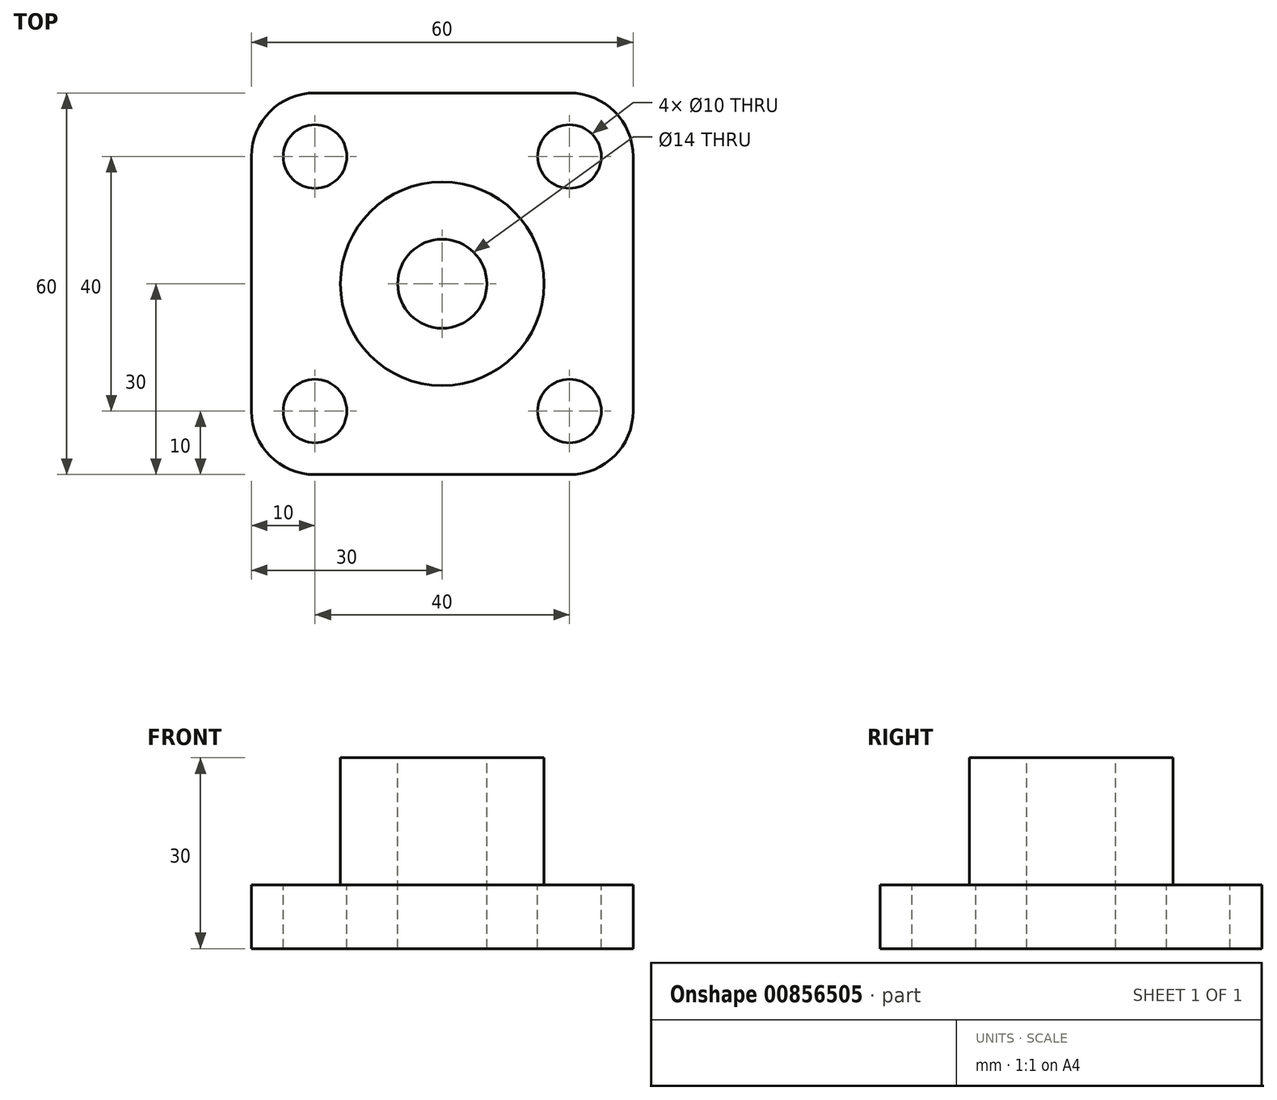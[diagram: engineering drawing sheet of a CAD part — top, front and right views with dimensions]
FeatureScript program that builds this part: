
annotation { "Feature Type Name" : "Feature", "Feature Type Description" : "" }
export const myFeature = defineFeature(function(context is Context, id is Id, definition is map)
    precondition{}
    {
        {
            var Q0;
            Q0=qCreatedBy(makeId("Top.planeOp"),FACE);
            var sketch = newSketch(context, id + "F0", { "sketchPlane" : qUnion([Q0])});
            skLineSegment(sketch, "E0.bottom", {"start": v(30, 30) * mm, "end": v(-30, 30) * mm});
            skLineSegment(sketch, "E0.top", {"start": v(30, -30) * mm, "end": v(-30, -30) * mm});
            skLineSegment(sketch, "E0.left", {"start": v(30, 30) * mm, "end": v(30, -30) * mm});
            skLineSegment(sketch, "E0.right", {"start": v(-30, 30) * mm, "end": v(-30, -30) * mm});
            skPoint(sketch, "E0.middle", {"position": v(0, 0) * mm});
            skSolve(sketch);
        }
        {
            var Q0;
            Q0 = qSketchRegion(id + "F0", true);
            var Q1;
            Q1=makeQuery(id+"F0.imprint","IMPRINT",FACE,{"disambiguationData":[TD([[makeQuery(id+"F0.imprint","IMPRINT",EDGE,{"derivedFrom":sQuery(id+"F0.wireOp",EDGE,"E0.bottom")}),1.0]])]});
            extrude(context, id + "F1", {"entities" : qUnion([Q0, Q1]), "endBound" : BoundingType.SYMMETRIC, "depth" : 10 * mm, "offsetDistance" : 25 * mm});
        }
        {
            var Q0;
            Q0=makeQuery(id+"F1.opExtrude","SWEPT_EDGE",EDGE,{"disambiguationData":[OSD([sQuery(id+"F0.wireOp",EDGE,"E0.bottom"),sQuery(id+"F0.wireOp",EDGE,"E0.right")])]});
            var Q1;
            Q1=makeQuery(id+"F1.opExtrude","SWEPT_EDGE",EDGE,{"disambiguationData":[OSD([sQuery(id+"F0.wireOp",EDGE,"E0.bottom"),sQuery(id+"F0.wireOp",EDGE,"E0.left")])]});
            var Q2;
            Q2=makeQuery(id+"F1.opExtrude","SWEPT_EDGE",EDGE,{"disambiguationData":[OSD([sQuery(id+"F0.wireOp",EDGE,"E0.top"),sQuery(id+"F0.wireOp",EDGE,"E0.left")])]});
            var Q3;
            Q3=makeQuery(id+"F1.opExtrude","SWEPT_EDGE",EDGE,{"disambiguationData":[OSD([sQuery(id+"F0.wireOp",EDGE,"E0.top"),sQuery(id+"F0.wireOp",EDGE,"E0.right")])]});
            fillet(context, id + "F2", {"entities" : qUnion([Q0, Q1, Q2, Q3]), "radius" : 10 * mm, "tangentPropagation" : true, "allowEdgeOverflow" : false});
        }
        {
            var Q0;
            Q0=makeQuery(id+"F1.opExtrude","CAP_FACE",FACE,{"disambiguationData":[OSD([sQuery(id+"F0.wireOp",EDGE,"E0.bottom"),sQuery(id+"F0.wireOp",EDGE,"E0.top"),sQuery(id+"F0.wireOp",EDGE,"E0.left"),sQuery(id+"F0.wireOp",EDGE,"E0.right")])],"isStart":false});
            var sketch = newSketch(context, id + "F3", { "sketchPlane" : qUnion([Q0])});
            skPoint(sketch, "E1", {"position": v(-20, 20) * mm});
            skPoint(sketch, "E2", {"position": v(20, 20) * mm});
            skPoint(sketch, "E3", {"position": v(20, -20) * mm});
            skPoint(sketch, "E4", {"position": v(-20, -20) * mm});
            skCircle(sketch, "E5", {"center": v(0, 0) * mm, "radius": 16 * mm});
            skSolve(sketch);
        }
        {
            var Q0;
            Q0=sQuery(id+"F3.wireOp",VERTEX,"E1");
            var Q1;
            Q1=sQuery(id+"F3.wireOp",VERTEX,"E2");
            var Q2;
            Q2=sQuery(id+"F3.wireOp",VERTEX,"E3");
            var Q3;
            Q3=sQuery(id+"F3.wireOp",VERTEX,"E4");
            var Q4;
            Q4=makeQuery(id+"F1.opExtrude","SWEPT_BODY",BODY,{"disambiguationData":[OSD([sQuery(id+"F0.wireOp",EDGE,"E0.bottom"),sQuery(id+"F0.wireOp",EDGE,"E0.top"),sQuery(id+"F0.wireOp",EDGE,"E0.left"),sQuery(id+"F0.wireOp",EDGE,"E0.right")])]});
            hole(context, id + "F4", {"style" : HoleStyle.SIMPLE, "endStyle" : HoleEndStyle.BLIND, "holeDiameter" : 10 * mm, "majorDiameter" : 16 * mm, "holeDepth" : 10 * mm, "isTappedThrough" : true, "tappedDepth" : 12 * mm, "tapClearance" : 3, "startFromSketch" : true, "locations" : qUnion([Q0, Q1, Q2, Q3]), "scope" : qUnion([Q4])});
        }
        {
            var Q0;
            Q0=makeQuery(id+"F3.imprint","IMPRINT",FACE,{"disambiguationData":[TD([[makeQuery(id+"F3.imprint","IMPRINT",EDGE,{"derivedFrom":sQuery(id+"F3.wireOp",EDGE,"E5")}),1.0]])]});
            extrude(context, id + "F5", {"entities" : qUnion([Q0]), "operationType" : NewBodyOperationType.ADD, "depth" : 20 * mm, "offsetDistance" : 25 * mm});
        }
        {
            var Q0;
            Q0=makeQuery(id+"F5.opExtrude","CAP_FACE",FACE,{"disambiguationData":[OSD([sQuery(id+"F3.wireOp",EDGE,"E5")])],"isStart":false});
            var sketch = newSketch(context, id + "F6", { "sketchPlane" : qUnion([Q0])});
            skPoint(sketch, "E6", {"position": v(0, 0) * mm});
            skSolve(sketch);
        }
        {
            var Q0;
            Q0=sQuery(id+"F6.wireOp",VERTEX,"E6");
            var Q1;
            Q1=makeQuery(id+"F1.opExtrude","SWEPT_BODY",BODY,{"disambiguationData":[OSD([sQuery(id+"F0.wireOp",EDGE,"E0.bottom"),sQuery(id+"F0.wireOp",EDGE,"E0.top"),sQuery(id+"F0.wireOp",EDGE,"E0.left"),sQuery(id+"F0.wireOp",EDGE,"E0.right")])]});
            hole(context, id + "F7", {"style" : HoleStyle.SIMPLE, "endStyle" : HoleEndStyle.THROUGH, "standardTappedOrClearance" : lookupTablePath({ "standard" : "ISO", "engagement" : "75%", "pitch" : "2 mm", "size" : "M16", "type" : "Tapped" }), "standardBlindInLast" : lookupTablePath({ "standard" : "ISO", "engagement" : "75%", "pitch" : "2 mm", "size" : "M16", "type" : "Tapped" }), "holeDiameter" : 14 * mm, "majorDiameter" : 16 * mm, "showTappedDepth" : true, "isTappedThrough" : true, "tappedDepth" : 12 * mm, "tapClearance" : 3, "startFromSketch" : true, "locations" : qUnion([Q0]), "scope" : qUnion([Q1])});
        }
    });
